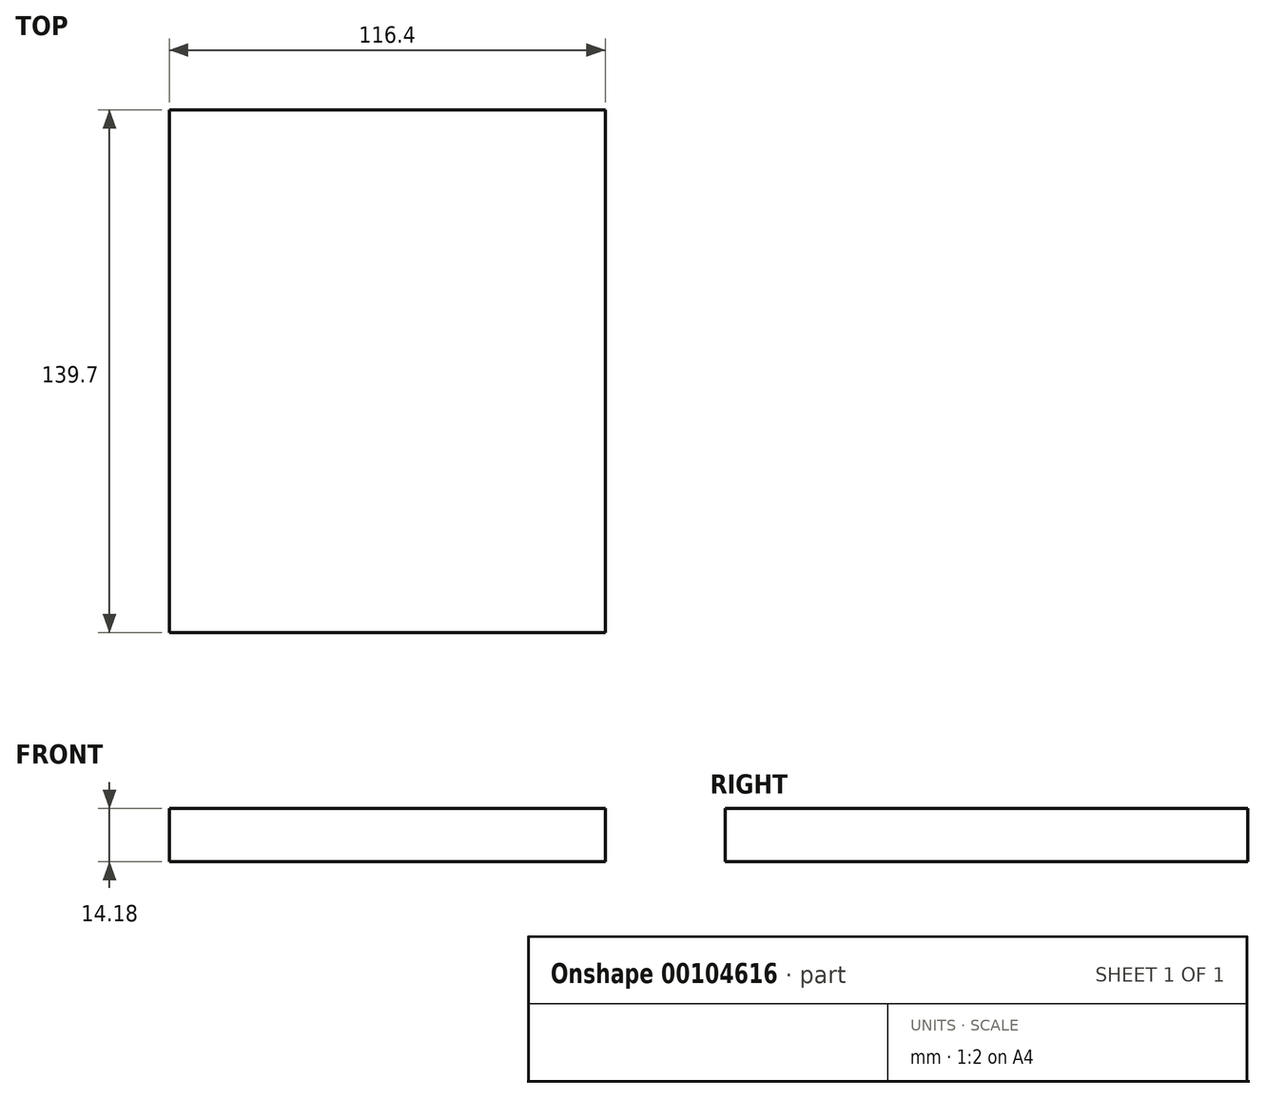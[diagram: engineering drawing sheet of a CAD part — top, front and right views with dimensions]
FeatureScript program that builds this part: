
annotation { "Feature Type Name" : "Feature", "Feature Type Description" : "" }
export const myFeature = defineFeature(function(context is Context, id is Id, definition is map)
    precondition{}
    {
        {
            var Q0;
            Q0=qCreatedBy(makeId("Front.planeOp"),FACE);
            var sketch = newSketch(context, id + "F0", { "sketchPlane" : qUnion([Q0])});
            skLineSegment(sketch, "E0.bottom", {"start": v(-58.2, -22.78) * mm, "end": v(58.2, -22.78) * mm});
            skLineSegment(sketch, "E0.top", {"start": v(-58.2, -36.96) * mm, "end": v(58.2, -36.96) * mm});
            skLineSegment(sketch, "E0.left", {"start": v(-58.2, -22.78) * mm, "end": v(-58.2, -36.96) * mm});
            skLineSegment(sketch, "E0.right", {"start": v(58.2, -22.78) * mm, "end": v(58.2, -36.96) * mm});
            skPoint(sketch, "E1", {"position": v(0, -36.96) * mm});
            skSolve(sketch);
        }
        {
            var Q0;
            Q0 = qSketchRegion(id + "F0", true);
            extrude(context, id + "F1", {"entities" : qUnion([Q0]), "depth" : 139.7 * mm});
        }
        {
            var Q0;
            Q0=qCreatedBy(makeId("Right.planeOp"),FACE);
            cPlane(context, id + "F2", {"entities" : qUnion([Q0]), "cplaneType" : CPlaneType.OFFSET, "offset" : 28.1 * mm, "oppositeDirection" : true, "width" : 152.4 * mm, "height" : 152.4 * mm});
        }
        {
            var Q0;
            Q0=makeQuery(id+"F1.opExtrude","SWEPT_FACE",FACE,{"disambiguationData":[OSD([sQuery(id+"F0.wireOp",EDGE,"E0.top")])]});
            var sketch = newSketch(context, id + "F3", { "sketchPlane" : qUnion([Q0])});
            skLineSegment(sketch, "E2.bottom", {"start": v(-38.73, 118.78) * mm, "end": v(38.73, 118.78) * mm});
            skLineSegment(sketch, "E2.top", {"start": v(-38.73, 42.58) * mm, "end": v(38.73, 42.58) * mm});
            skLineSegment(sketch, "E2.left", {"start": v(-38.74, 118.78) * mm, "end": v(-38.74, 42.58) * mm});
            skLineSegment(sketch, "E2.right", {"start": v(38.73, 118.78) * mm, "end": v(38.73, 42.58) * mm});
            skPoint(sketch, "E3", {"position": v(0, 118.78) * mm});
            skLineSegment(sketch, "E4.bottom", {"start": v(-58.2, 0) * mm, "end": v(-32.8, 0) * mm});
            skLineSegment(sketch, "E4.top", {"start": v(-58.2, 38.1) * mm, "end": v(-32.8, 38.1) * mm});
            skLineSegment(sketch, "E4.left", {"start": v(-58.2, 0) * mm, "end": v(-58.2, 38.1) * mm});
            skLineSegment(sketch, "E4.right", {"start": v(-32.8, 0) * mm, "end": v(-32.8, 38.1) * mm});
            skLineSegment(sketch, "E5.bottom", {"start": v(58.2, 0) * mm, "end": v(32.8, 0) * mm});
            skLineSegment(sketch, "E5.top", {"start": v(58.2, 38.1) * mm, "end": v(32.8, 38.1) * mm});
            skLineSegment(sketch, "E5.left", {"start": v(58.2, 0) * mm, "end": v(58.2, 38.1) * mm});
            skLineSegment(sketch, "E5.right", {"start": v(32.8, 0) * mm, "end": v(32.8, 38.1) * mm});
            skSolve(sketch);
        }
    });
